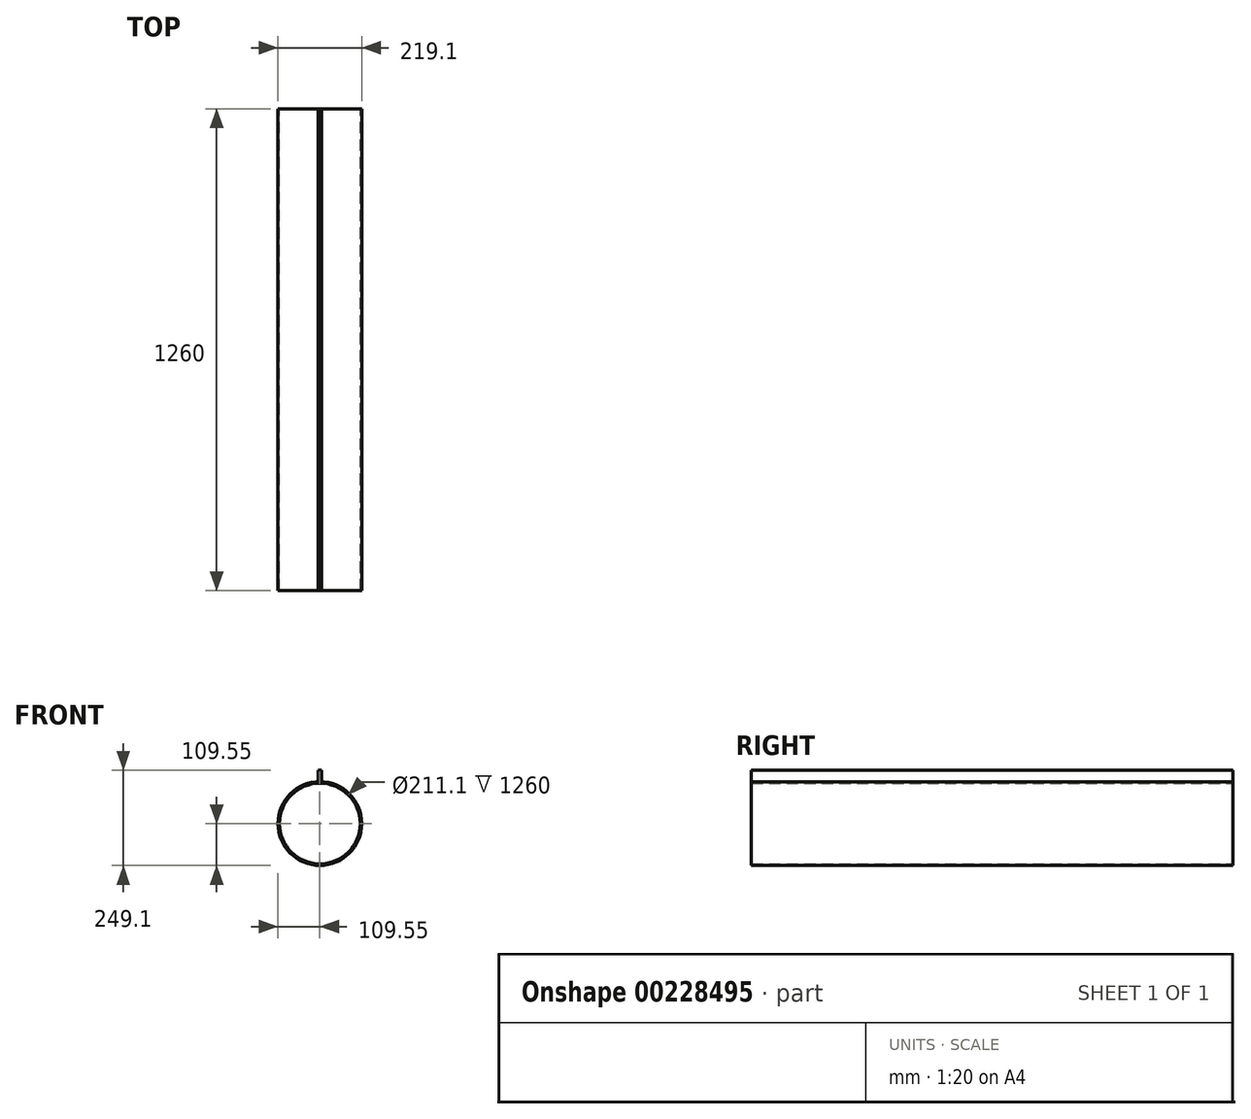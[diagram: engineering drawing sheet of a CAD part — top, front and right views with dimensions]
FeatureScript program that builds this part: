
annotation { "Feature Type Name" : "Feature", "Feature Type Description" : "" }
export const myFeature = defineFeature(function(context is Context, id is Id, definition is map)
    precondition{}
    {
        {
            assignVariable(context, id + "F0", {"name" : "L", "anyValue" : 1260});
        }
        {
            var Q0;
            Q0=qCreatedBy(makeId("Front.planeOp"),FACE);
            var sketch = newSketch(context, id + "F1", { "sketchPlane" : qUnion([Q0])});
            skCircle(sketch, "E0", {"center": v(0, 0) * mm, "radius": 109.55 * mm});
            skCircle(sketch, "E1.0", {"center": v(0, 0) * mm, "radius": 105.55 * mm});
            skLineSegment(sketch, "E2.bottom", {"start": v(-5, 139.55) * mm, "end": v(5, 139.55) * mm});
            skLineSegment(sketch, "E2.top", {"start": v(-5, 109.55) * mm, "end": v(5, 109.55) * mm});
            skLineSegment(sketch, "E2.left", {"start": v(-5, 139.55) * mm, "end": v(-5, 109.55) * mm});
            skLineSegment(sketch, "E2.right", {"start": v(5, 139.55) * mm, "end": v(5, 109.55) * mm});
            skPoint(sketch, "E2.middle", {"position": v(0, 124.55) * mm});
            skSolve(sketch);
        }
        {
            var Q0;
            Q0=makeQuery(id+"F1.imprint","IMPRINT",FACE,{"disambiguationData":[TD([[makeQuery(id+"F1.imprint","IMPRINT",EDGE,{"derivedFrom":sQuery(id+"F1.wireOp",EDGE,"E0")}),1.0]])]});
            extrude(context, id + "F2", {"entities" : qUnion([Q0]), "depth" : (getVariable(context, 'L')) * mm, "hasSecondDirection" : true, "secondDirectionOppositeDirection" : true, "secondDirectionDepth" : 25 * mm, "symmetric" : true});
        }
        {
            var Q0;
            Q0=makeQuery(id+"F1.imprint","IMPRINT",FACE,{"disambiguationData":[TD([[makeQuery(id+"F1.imprint","IMPRINT",EDGE,{"derivedFrom":sQuery(id+"F1.wireOp",EDGE,"E2.bottom")}),-1.0]])]});
            var Q1;
            Q1=makeQuery(id+"F2.opExtrude","CAP_FACE",FACE,{"disambiguationData":[OSD([sQuery(id+"F1.wireOp",EDGE,"E0"),sQuery(id+"F1.wireOp",EDGE,"E1.0")])],"isStart":false});
            var Q2;
            Q2=makeQuery(id+"F2.opExtrude","CAP_FACE",FACE,{"disambiguationData":[OSD([sQuery(id+"F1.wireOp",EDGE,"E0"),sQuery(id+"F1.wireOp",EDGE,"E1.0")])],"isStart":true});
            extrude(context, id + "F3", {"entities" : qUnion([Q0]), "endBound" : BoundingType.UP_TO_SURFACE, "endBoundEntityFace" : qUnion([Q1]), "depth" : 25 * mm, "hasSecondDirection" : true, "secondDirectionBound" : BoundingType.UP_TO_SURFACE, "secondDirectionOppositeDirection" : true, "secondDirectionBoundEntityFace" : qUnion([Q2]), "secondDirectionDepth" : 25 * mm});
        }
    });
